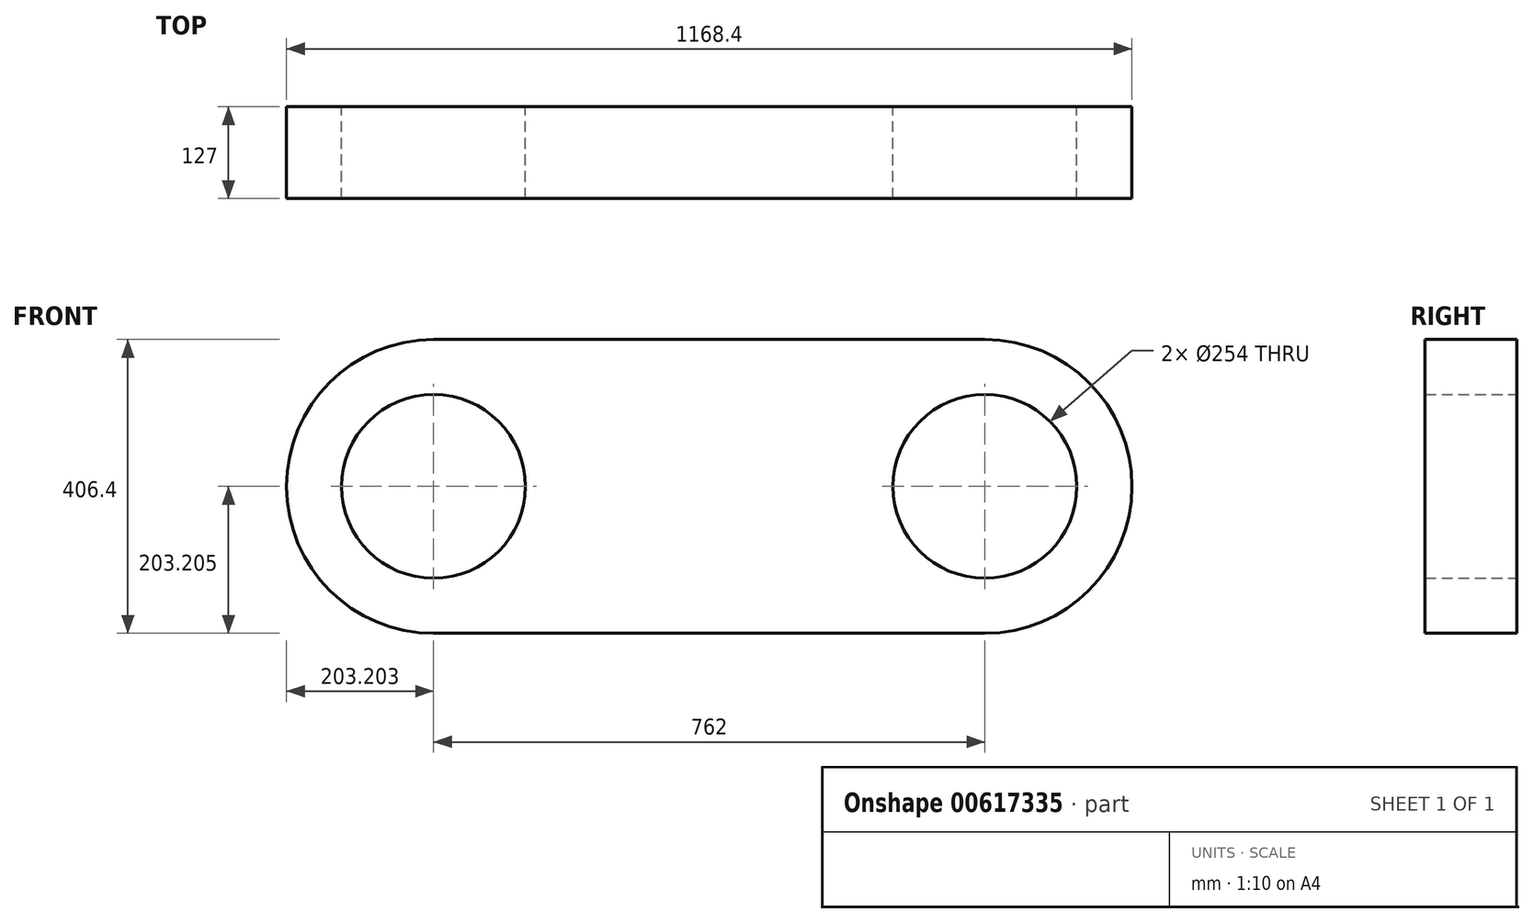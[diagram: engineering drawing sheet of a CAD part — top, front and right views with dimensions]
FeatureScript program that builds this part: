
annotation { "Feature Type Name" : "Feature", "Feature Type Description" : "" }
export const myFeature = defineFeature(function(context is Context, id is Id, definition is map)
    precondition{}
    {
        {
            var Q0;
            Q0=qCreatedBy(makeId("Front.planeOp"),FACE);
            var sketch = newSketch(context, id + "F0", { "sketchPlane" : qUnion([Q0])});
            skLineSegment(sketch, "E0.bottom", {"start": v(-379.14, 206) * mm, "end": v(382.86, 206) * mm});
            skLineSegment(sketch, "E0.top", {"start": v(-379.14, -200.4) * mm, "end": v(382.86, -200.4) * mm});
            skLineSegment(sketch, "E0.right", {"start": v(382.86, 2.8) * mm, "end": v(382.86, 0) * mm});
            skArc(sketch, "E1", {"start": v(-379.14, 206) * mm, "mid": v(-582.34, 2.8) * mm, "end": v(-379.14, -200.4) * mm});
            skPoint(sketch, "E2.centerSnap0", {"position": v(382.86, 2.8) * mm});
            skArc(sketch, "E3", {"start": v(382.86, -200.4) * mm, "mid": v(586.06, 2.8) * mm, "end": v(382.86, 206) * mm});
            skCircle(sketch, "E4", {"center": v(-379.14, 2.8) * mm, "radius": 127 * mm});
            skCircle(sketch, "E5", {"center": v(382.86, 2.8) * mm, "radius": 127 * mm});
            skSolve(sketch);
        }
        {
            var Q0;
            Q0 = qSketchRegion(id + "F0", true);
            extrude(context, id + "F1", {"entities" : qUnion([Q0]), "endBound" : BoundingType.SYMMETRIC, "depth" : 127 * mm, "offsetDistance" : 25.4 * mm});
        }
    });
